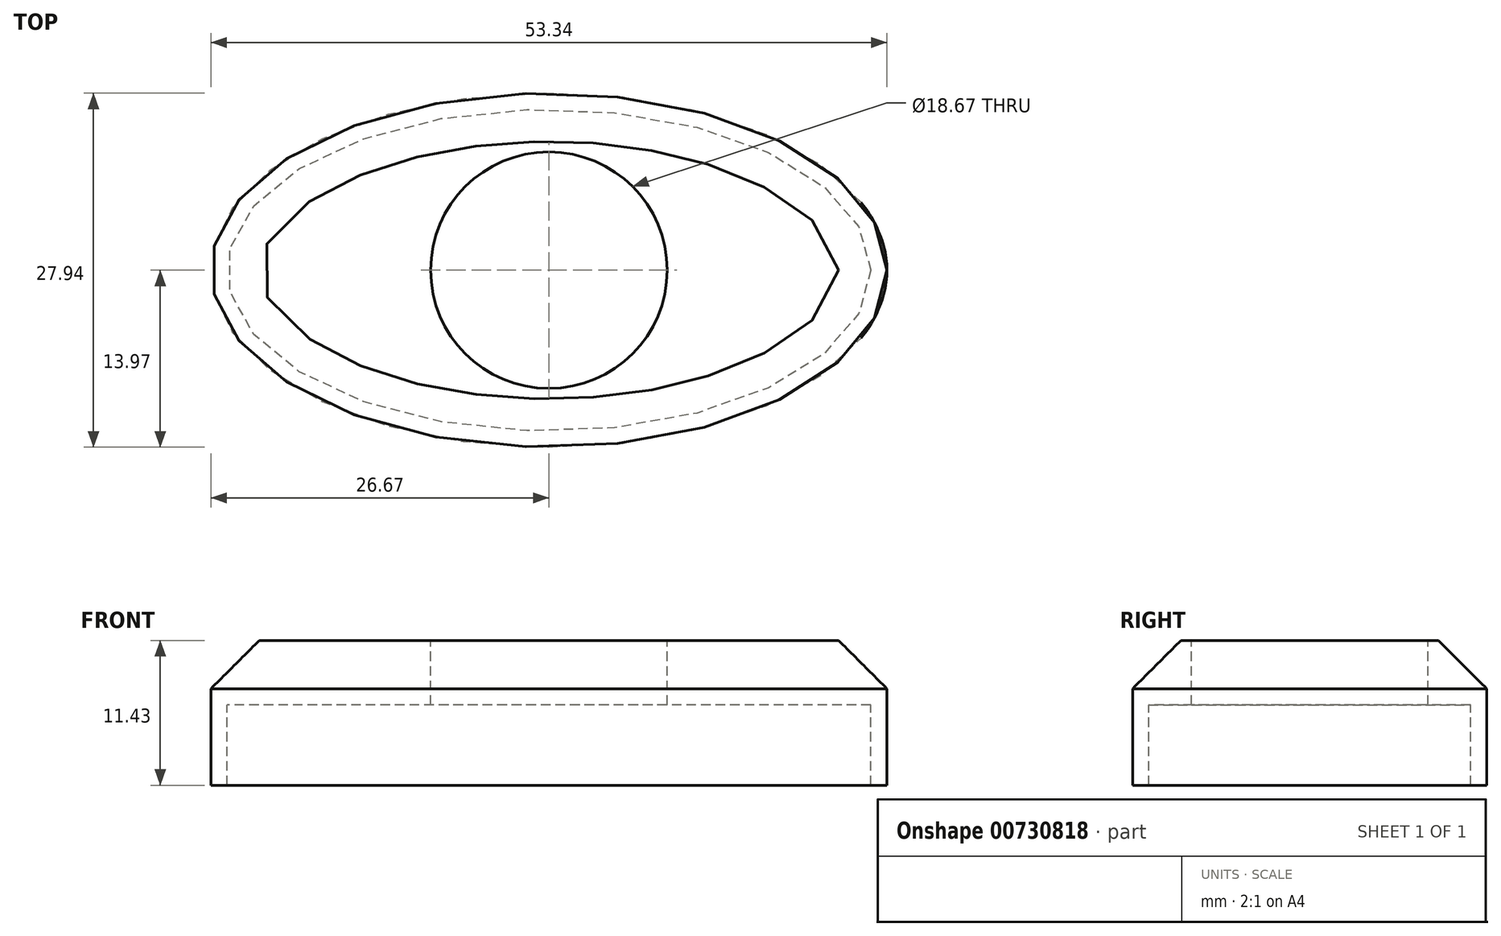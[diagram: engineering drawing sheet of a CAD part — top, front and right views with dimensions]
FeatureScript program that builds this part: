
annotation { "Feature Type Name" : "Feature", "Feature Type Description" : "" }
export const myFeature = defineFeature(function(context is Context, id is Id, definition is map)
    precondition{}
    {
        {
            var Q0;
            Q0=qCreatedBy(makeId("Top.planeOp"),FACE);
            var sketch = newSketch(context, id + "F0", { "sketchPlane" : qUnion([Q0])});
            skEllipse(sketch, "E0", {"center": v(0, 0) * mm, "majorRadius": 26.67 * mm, "minorRadius": 13.97 * mm, "majorAxis": v(1, 0)});
            skSolve(sketch);
        }
        {
            var Q0;
            Q0=makeQuery(id+"F0.imprint","IMPRINT",FACE,{"disambiguationData":[TD([[makeQuery(id+"F0.imprint","IMPRINT",EDGE,{"derivedFrom":sQuery(id+"F0.wireOp",EDGE,"E0")}),1.0]])]});
            extrude(context, id + "F1", {"entities" : qUnion([Q0]), "depth" : 5.08 * mm, "offsetDistance" : 25.4 * mm});
        }
        {
            var Q0;
            Q0=makeQuery(id+"F1.opExtrude","CAP_FACE",FACE,{"disambiguationData":[OSD([sQuery(id+"F0.wireOp",EDGE,"E0")])],"isStart":true});
            var sketch = newSketch(context, id + "F2", { "sketchPlane" : qUnion([Q0])});
            skEllipse(sketch, "E1", {"center": v(0, 0) * mm, "majorRadius": 25.4 * mm, "minorRadius": 12.7 * mm, "majorAxis": v(1, 0)});
            skEllipse(sketch, "E2", {"center": v(0, 0) * mm, "majorRadius": 26.67 * mm, "minorRadius": 13.97 * mm, "majorAxis": v(1, 0)});
            skSolve(sketch);
        }
        {
            var Q0;
            Q0=makeQuery(id+"F2.imprint","IMPRINT",FACE,{"disambiguationData":[TD([[makeQuery(id+"F2.imprint","IMPRINT",EDGE,{"derivedFrom":sQuery(id+"F2.wireOp",EDGE,"E1")}),-1.0]])]});
            extrude(context, id + "F3", {"entities" : qUnion([Q0]), "operationType" : NewBodyOperationType.ADD, "depth" : 6.35 * mm, "offsetDistance" : 25.4 * mm});
        }
        {
            var Q0;
            Q0=makeQuery(id+"F1.opExtrude","CAP_EDGE",EDGE,{"disambiguationData":[OSD([sQuery(id+"F0.wireOp",EDGE,"E0")])],"isStart":false});
            chamfer(context, id + "F4", {"entities" : qUnion([Q0]), "width" : 3.8 * mm, "tangentPropagation" : true});
        }
        {
            var Q0;
            Q0=makeQuery(id+"F1.opExtrude","CAP_FACE",FACE,{"disambiguationData":[OSD([sQuery(id+"F0.wireOp",EDGE,"E0")])],"isStart":false});
            var sketch = newSketch(context, id + "F5", { "sketchPlane" : qUnion([Q0])});
            skCircle(sketch, "E3", {"center": v(0, 0) * mm, "radius": 9.33 * mm});
            skSolve(sketch);
        }
        {
            var Q0;
            Q0=makeQuery(id+"F5.imprint","IMPRINT",FACE,{"disambiguationData":[TD([[makeQuery(id+"F5.imprint","IMPRINT",EDGE,{"derivedFrom":sQuery(id+"F5.wireOp",EDGE,"E3")}),1.0]])]});
            extrude(context, id + "F6", {"entities" : qUnion([Q0]), "operationType" : NewBodyOperationType.REMOVE, "oppositeDirection" : true, "depth" : 25.4 * mm, "offsetDistance" : 25.4 * mm});
        }
    });
